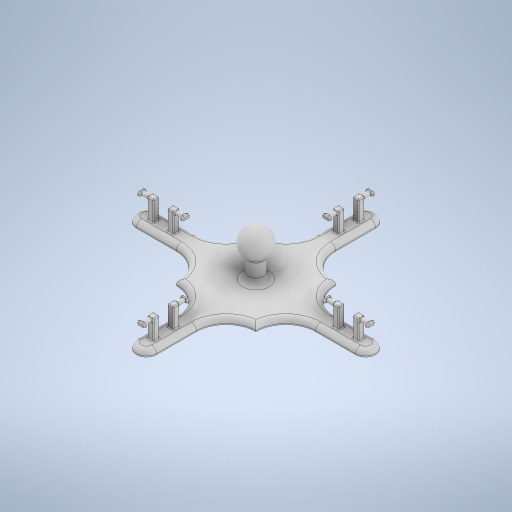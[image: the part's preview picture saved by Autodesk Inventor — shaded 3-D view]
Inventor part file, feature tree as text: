
AUTODESK INVENTOR PART (.ipt)
format: ipt  version: 2023 (Build 270158000, 158)  size: 1,412,608 bytes
history: native  units: mm
features: sketch x14, other x9, extrude x7, fillet x7, revolve x1, mirror x1, pattern_circular x1
ambient origin geometry x8: Origin, YZ Plane, XZ Plane, XY Plane, X Axis, Y Axis, Z Axis, Center Point
bodies: Body1 (feature_tree)
feature tree (40):
  other  "Bryła1"
  sketch  "Szkic1"
  extrude  "Wyciągnięcie proste1"  Depth=80.0mm
  fillet  "Zaokrąglenie6"  Radius=80.0mm
  other  "Zaokrąglenie powierzchni9"
  other  "Zaokrąglenie powierzchni10"
  other  "Zaokrąglenie powierzchni11"
  other  "Zaokrąglenie powierzchni12"
  other  "Zaokrąglenie powierzchni13"
  other  "Zaokrąglenie powierzchni14"
  other  "Zaokrąglenie powierzchni15"
  other  "Zaokrąglenie powierzchni16"
  fillet  "Zaokrąglenie7"  Radius=6.0mm
  extrude  "Wyciągnięcie proste8"  Depth=20.0mm
  sketch  "Szkic10"
  sketch  "Szkic11"
  revolve  "Obrót1"
  fillet  "Zaokrąglenie10"  Radius=20.0mm
  fillet  "Zaokrąglenie11"  Radius=20.0mm
  extrude  "Wyciągnięcie proste9"  Depth=20.0mm
  sketch  "Szkic18"
  extrude  "Wyciągnięcie proste11"  Depth=10.0mm
  sketch  "Szkic20"
  extrude  "Wyciągnięcie proste12"  Depth=10.0mm
  fillet  "Zaokrąglenie16"  Radius=80.0mm
  extrude  "Wyciągnięcie proste13"  Depth=80.0mm
  extrude  "Wyciągnięcie proste14"  Depth=80.0mm
  fillet  "Zaokrąglenie17"  Radius=80.0mm
  fillet  "Zaokrąglenie18"  Radius=10.0mm
  mirror  "Odbij3"
  pattern_circular  "Szyk kołowy1"  Count=3  [1 undecoded]
  sketch  "Szkic24"
  sketch  "Szkic2"
  sketch  "Szkic9"
  sketch  "Szkic12"
  sketch  "Szkic13"
  sketch  "Szkic19"
  sketch  "Szkic21"
  sketch  "Szkic22"
  sketch  "Szkic23"
note: 1 required parameter value undecoded (feature->parameter linkage not recoverable at this tier; creation-order binding heuristic only, values carry confidence <= 0.55)
